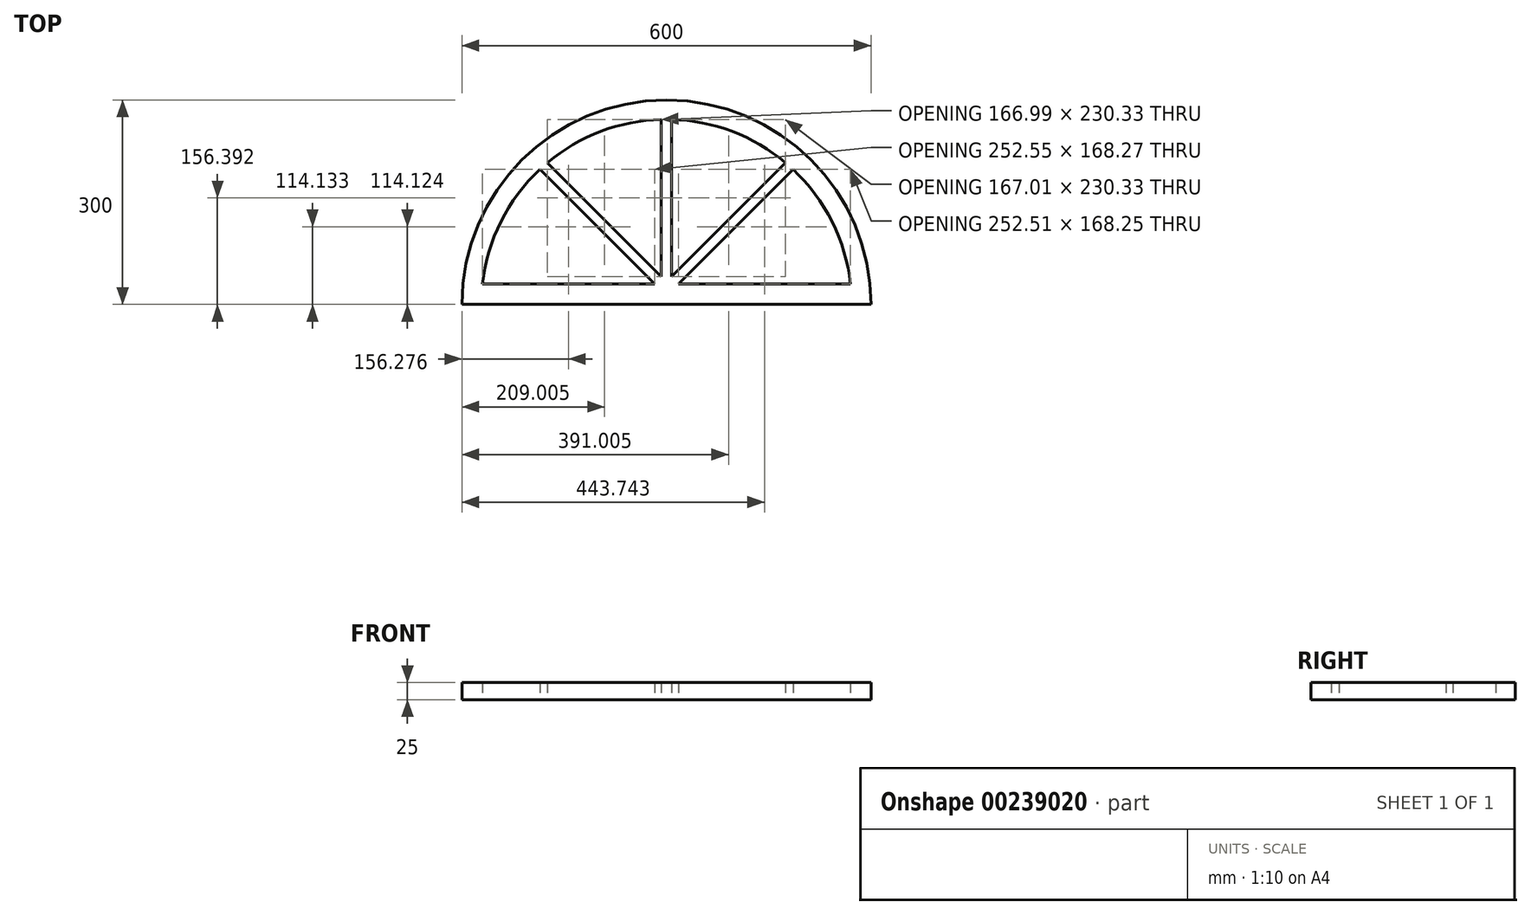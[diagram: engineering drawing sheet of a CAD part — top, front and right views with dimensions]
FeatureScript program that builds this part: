
annotation { "Feature Type Name" : "Feature", "Feature Type Description" : "" }
export const myFeature = defineFeature(function(context is Context, id is Id, definition is map)
    precondition{}
    {
        {
            var Q0;
            Q0=qCreatedBy(makeId("Top.planeOp"),FACE);
            var sketch = newSketch(context, id + "F0", { "sketchPlane" : qUnion([Q0])});
            skArc(sketch, "E0", {"start": v(270, 30) * mm, "mid": v(242.9, 121.65) * mm, "end": v(185.74, 198.25) * mm});
            skArc(sketch, "E1", {"start": v(300, 0) * mm, "mid": v(0, 300) * mm, "end": v(-300, 0) * mm});
            skLineSegment(sketch, "E2", {"start": v(-300, 0) * mm, "end": v(300, 0) * mm});
            skPoint(sketch, "E3.end.orphan", {"position": v(-267.07, 0) * mm});
            skPoint(sketch, "E4.end.orphan", {"position": v(267.07, 0) * mm});
            skLineSegment(sketch, "E5", {"start": v(17.49, 30) * mm, "end": v(270, 30) * mm});
            skLineSegment(sketch, "E6", {"start": v(-17.45, 30) * mm, "end": v(-270, 30) * mm});
            skLineSegment(sketch, "E7", {"start": v(17.49, 30) * mm, "end": v(185.74, 198.25) * mm});
            skLineSegment(sketch, "E8", {"start": v(185.74, 198.25) * mm, "end": v(17.49, 30) * mm});
            skLineSegment(sketch, "E9", {"start": v(-17.45, 30) * mm, "end": v(-185.72, 198.27) * mm});
            skLineSegment(sketch, "E10", {"start": v(-185.72, 198.27) * mm, "end": v(-17.45, 30) * mm});
            skLineSegment(sketch, "E11", {"start": v(7.5, 271.56) * mm, "end": v(7.5, 41.23) * mm});
            skLineSegment(sketch, "E12", {"start": v(7.5, 41.23) * mm, "end": v(7.5, 271.56) * mm});
            skLineSegment(sketch, "E13", {"start": v(-7.5, 271.56) * mm, "end": v(-7.5, 41.23) * mm});
            skArc(sketch, "E14.trimOffspring", {"start": v(-7.5, 271.56) * mm, "mid": v(-96.35, 254) * mm, "end": v(-174.49, 208.22) * mm});
            skLineSegment(sketch, "E15", {"start": v(-7.5, 41.23) * mm, "end": v(-174.49, 208.22) * mm});
            skLineSegment(sketch, "E16", {"start": v(7.5, 41.23) * mm, "end": v(174.5, 208.2) * mm});
            skLineSegment(sketch, "E17", {"start": v(174.5, 208.2) * mm, "end": v(7.5, 41.23) * mm});
            skArc(sketch, "E18.trimOffspring", {"start": v(-185.72, 198.27) * mm, "mid": v(-242.9, 121.67) * mm, "end": v(-270, 30) * mm});
            skArc(sketch, "E19.trimOffspring", {"start": v(174.5, 208.2) * mm, "mid": v(96.36, 254) * mm, "end": v(7.5, 271.56) * mm});
            skSolve(sketch);
        }
        {
            var Q0;
            Q0 = qSketchRegion(id + "F0", true);
            extrude(context, id + "F1", {"entities" : qUnion([Q0]), "depth" : 25 * mm});
        }
    });
